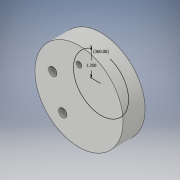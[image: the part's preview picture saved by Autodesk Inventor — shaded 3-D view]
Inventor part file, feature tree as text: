
AUTODESK INVENTOR PART (.ipt)
format: ipt  version: 2018 (Build 220112000, 112)  size: 123,392 bytes
history: native  units: in
note: dims shown in document units (in); Inventor stores cm internally (conversion verified against a paired STEP export)
features: sketch x2, hole x2, extrude x1
ambient origin geometry x8: Origin, YZ Plane, XZ Plane, XY Plane, X Axis, Y Axis, Z Axis, Center Point
bodies: Body1 (feature_tree)
feature tree (5):
  extrude  "Extrusion2"  Depth=2.5in
  sketch  "Sketch4"  dims[d9=1.0in d10=0.0in d12=1.25in d13=1.9685in d15=360.0deg d17=0.25in d18=0.75in d19=0.375in d20=0.25in d21=0.5635in d22=1.25in d23=0.8108in d24=0.375in d25=0.75in d26=0.75in d27=0.25in d28=0.5635in d29=1.25in d30=0.8108in d11=1.0in]
  hole  "Hole1"  [1 undecoded]
  hole  "Hole2"  [1 undecoded]
  sketch  "Sketch1"  dims[d0=4.0in d1=2.5in]
note: 2 required parameter values undecoded (feature->parameter linkage not recoverable at this tier; creation-order binding heuristic only, values carry confidence <= 0.55)
